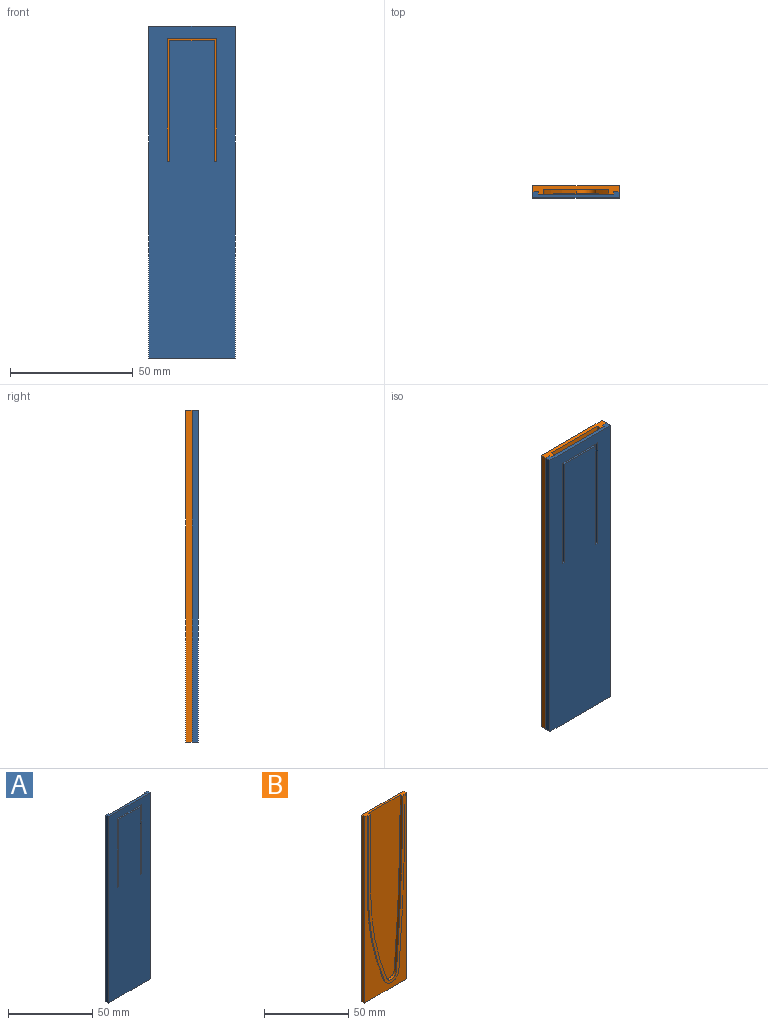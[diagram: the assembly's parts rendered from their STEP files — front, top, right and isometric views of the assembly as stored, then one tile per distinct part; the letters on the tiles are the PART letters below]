
ASSEMBLY  parts=2 mates=1
PART A: 20 faces, bbox 35x2.5x135 mm
  f0: plane 130.2x30.75mm, normal (0,1,0), area 3202.2mm2, adj f1,f7,f8,f9,f10,f11,f12,f13
  f1: plane 35x2.5mm, normal (0,0,1), area 56.8mm2, adj f0,f2,f4,f5,f6,f7,f8
  f2: plane 135x2.5mm, normal (-1,0,0), area 337.5mm2, adj f1,f3,f5,f6
  f3: plane 35x2.5mm, normal (0,0,-1), area 87.5mm2, adj f2,f4,f5,f6
  f4: plane 135x2.5mm, normal (1,0,0), area 337.5mm2, adj f1,f3,f5,f6
  f5: plane 135x35mm, normal (0,-1,0), area 4607mm2, adj f1,f2,f3,f4,f11,f12,f13,f14
  f6: plane 135x35mm, normal (0,1,0), area 1348.6mm2, adj f1,f2,f3,f4,f7,f8,f9,f10
  f7: cylinder r=1501.59mm len=124.51mm, axis (0,1,0), area 124.7mm2, adj f0,f1,f6,f10
  f8: plane 56x1mm, normal (1,0,0), area 56mm2, adj f0,f1,f6,f9
  f9: cylinder r=187.22mm len=70.33mm, axis (0,1,0), area 72.1mm2, adj f0,f6,f8,f10
  f10: cylinder r=6.2mm len=11.93mm, axis (0,1,0), area 16.6mm2, adj f0,f6,f7,f9
  f11: plane 1.5x1mm, normal (0,0,1), area 1.5mm2, adj f0,f5,f12,f18
  f12: plane 50x1.5mm, normal (1,0,0), area 75mm2, adj f0,f5,f11,f13
  f13: plane 20x1.5mm, normal (0,0,-1), area 30mm2, adj f0,f5,f12,f14
  f14: plane 50x1.5mm, normal (-1,0,0), area 75mm2, adj f0,f5,f13,f15
  f15: plane 1.5x1mm, normal (0,0,1), area 1.5mm2, adj f0,f5,f14,f16
  f16: plane 49x1.75mm, normal (1,0,0), area 74mm2, adj f0,f5,f15,f17,f19
  f17: plane 18x1.5mm, normal (0,0,1), area 27mm2, adj f5,f16,f18,f19
  f18: plane 49x1.75mm, normal (-1,0,0), area 74mm2, adj f0,f5,f11,f17,f19
  f19: cylinder r=5mm len=18mm, axis (-1,0,0), area 57.2mm2, adj f0,f16,f17,f18
PART B: 16 faces, bbox 35x3.5x135 mm
  f0: plane 135x35mm, normal (0,-1,0), area 1348.6mm2, adj f2,f3,f4,f5,f11,f12,f13,f14
  f1: plane 128.2x26.75mm, normal (0,-1,0), area 2844mm2, adj f2,f7,f8,f9,f10
  f2: plane 35x3.5mm, normal (0,0,1), area 64.8mm2, adj f0,f1,f3,f5,f6,f7,f10,f11
  f3: plane 135x2.5mm, normal (-1,0,0), area 337.5mm2, adj f0,f2,f4,f6
  f4: plane 35x2.5mm, normal (0,0,-1), area 87.5mm2, adj f0,f3,f5,f6
  f5: plane 135x2.5mm, normal (1,0,0), area 337.5mm2, adj f0,f2,f4,f6
  f6: plane 135x35mm, normal (0,1,0), area 4725mm2, adj f2,f3,f4,f5
  f7: cylinder r=1499.59mm len=124.35mm, axis (0,1,0), area 249mm2, adj f1,f2,f8,f15
  f8: cylinder r=4.2mm len=8.08mm, axis (0,1,0), area 22.5mm2, adj f1,f7,f9,f15
  f9: cylinder r=185.22mm len=69.57mm, axis (0,1,0), area 142.6mm2, adj f1,f8,f10,f15
  f10: plane 56x2mm, normal (1,0,0), area 112mm2, adj f1,f2,f9,f15
  f11: plane 56x1mm, normal (-1,0,0), area 56mm2, adj f0,f2,f12,f15
  f12: cylinder r=187.22mm len=70.33mm, axis (0,1,0), area 72.1mm2, adj f0,f11,f13,f15
  f13: cylinder r=6.2mm len=11.93mm, axis (0,1,0), area 16.6mm2, adj f0,f12,f14,f15
  f14: cylinder r=1501.59mm len=124.51mm, axis (0,1,0), area 124.7mm2, adj f0,f2,f13,f15
  f15: plane 130.2x30.75mm, normal (0,-1,0), area 532.4mm2, adj f2,f7,f8,f9,f10,f11,f12,f13
PLACE A t=(0,-1,0)mm
PLACE B at identity fixed
MATE fastened B.f2 <-> A.f1  axis (0,0,1) through (0,0,0)mm
